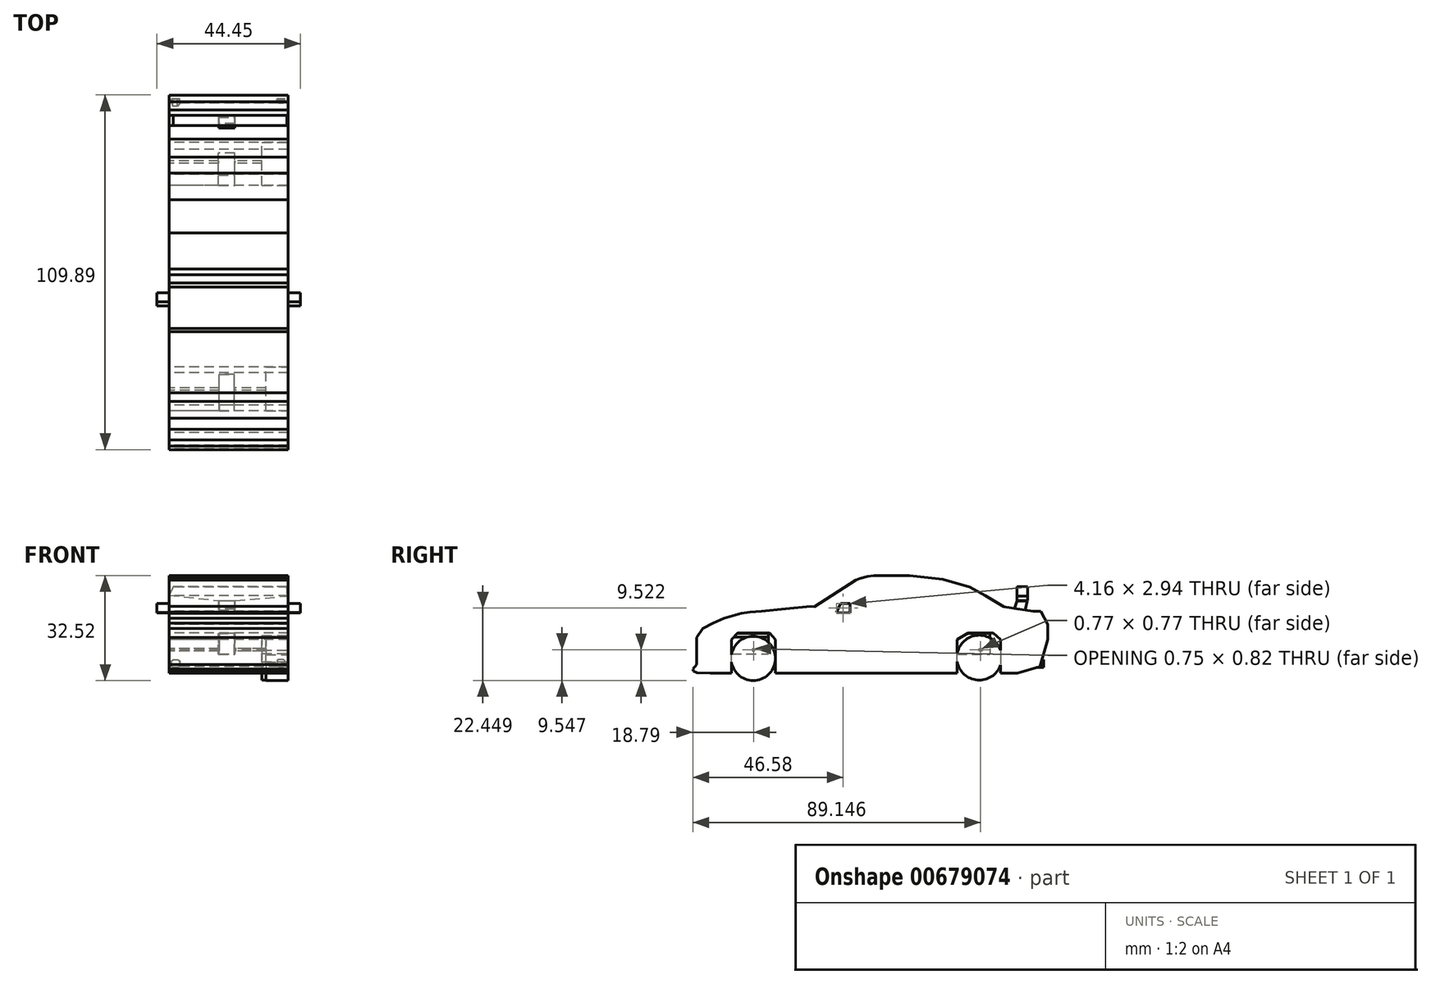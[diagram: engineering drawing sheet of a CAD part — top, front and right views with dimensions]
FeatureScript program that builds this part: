
annotation { "Feature Type Name" : "Feature", "Feature Type Description" : "" }
export const myFeature = defineFeature(function(context is Context, id is Id, definition is map)
    precondition{}
    {
        {
            var Q0;
            Q0=qCreatedBy(makeId("Right.planeOp"),FACE);
            var sketch = newSketch(context, id + "F0", { "sketchPlane" : qUnion([Q0])});
            skLineSegment(sketch, "E0", {"start": v(53.3, 2.94) * mm, "end": v(60.21, 4.98) * mm});
            skLineSegment(sketch, "E1", {"start": v(60.21, 4.98) * mm, "end": v(62.65, 13.3) * mm});
            skLineSegment(sketch, "E2", {"start": v(58.05, 22.1) * mm, "end": v(52.83, 22.89) * mm});
            skLineSegment(sketch, "E3", {"start": v(43.36, 26.9) * mm, "end": v(38.48, 29.55) * mm});
            skLineSegment(sketch, "E4", {"start": v(38.48, 29.55) * mm, "end": v(30.16, 31.98) * mm});
            skLineSegment(sketch, "E5", {"start": v(30.16, 31.98) * mm, "end": v(19.87, 33.17) * mm});
            skLineSegment(sketch, "E6", {"start": v(19.87, 33.17) * mm, "end": v(8.77, 33.17) * mm});
            skLineSegment(sketch, "E7", {"start": v(8.77, 33.17) * mm, "end": v(6.96, 32.93) * mm});
            skLineSegment(sketch, "E8", {"start": v(6.96, 32.93) * mm, "end": v(4.48, 32.32) * mm});
            skLineSegment(sketch, "E9", {"start": v(4.48, 32.32) * mm, "end": v(3.18, 31.74) * mm});
            skLineSegment(sketch, "E10", {"start": v(-26.9, 22.15) * mm, "end": v(-32.22, 21.43) * mm});
            skLineSegment(sketch, "E11", {"start": v(-32.22, 21.43) * mm, "end": v(-37.52, 19.89) * mm});
            skLineSegment(sketch, "E12", {"start": v(-39.67, 2.94) * mm, "end": v(-41.9, 2.94) * mm});
            skLineSegment(sketch, "E13", {"start": v(58.05, 22.1) * mm, "end": v(58.25, 23.46) * mm});
            skLineSegment(sketch, "E14", {"start": v(58.25, 23.46) * mm, "end": v(53.04, 24.24) * mm});
            skLineSegment(sketch, "E15", {"start": v(53.04, 24.24) * mm, "end": v(52.83, 22.89) * mm});
            skPoint(sketch, "E16.endSnap0", {"position": v(40.92, 28.23) * mm});
            skPoint(sketch, "E17.start.orphan", {"position": v(61.15, 28.23) * mm});
            skLineSegment(sketch, "E18", {"start": v(-31.65, 2.94) * mm, "end": v(-31.65, 2.94) * mm});
            skLineSegment(sketch, "E19", {"start": v(-39.67, 2.94) * mm, "end": v(-35.23, 2.94) * mm});
            skLineSegment(sketch, "E20", {"start": v(-35.23, 2.94) * mm, "end": v(-35.23, 13.3) * mm});
            skLineSegment(sketch, "E21", {"start": v(-35.23, 13.3) * mm, "end": v(-33.4, 15.33) * mm});
            skLineSegment(sketch, "E22", {"start": v(-33.4, 15.33) * mm, "end": v(-23.45, 15.33) * mm});
            skLineSegment(sketch, "E23", {"start": v(-23.45, 15.33) * mm, "end": v(-21.63, 13.3) * mm});
            skLineSegment(sketch, "E24", {"start": v(-21.63, 13.3) * mm, "end": v(-21.63, 2.94) * mm});
            skLineSegment(sketch, "E25", {"start": v(-21.63, 2.94) * mm, "end": v(34.62, 2.94) * mm});
            skLineSegment(sketch, "E26", {"start": v(34.62, 2.94) * mm, "end": v(34.62, 13.3) * mm});
            skLineSegment(sketch, "E27", {"start": v(34.62, 13.3) * mm, "end": v(38.08, 15.33) * mm});
            skLineSegment(sketch, "E28", {"start": v(38.08, 15.33) * mm, "end": v(45.8, 15.33) * mm});
            skLineSegment(sketch, "E29", {"start": v(45.8, 15.33) * mm, "end": v(48.03, 13.3) * mm});
            skLineSegment(sketch, "E30", {"start": v(48.03, 13.3) * mm, "end": v(48.03, 2.94) * mm});
            skLineSegment(sketch, "E31", {"start": v(48.03, 2.94) * mm, "end": v(53.3, 2.94) * mm});
            skLineSegment(sketch, "E32", {"start": v(62.65, 13.3) * mm, "end": v(62.65, 18.08) * mm});
            skLineSegment(sketch, "E33", {"start": v(62.65, 18.08) * mm, "end": v(60.52, 22.13) * mm});
            skLineSegment(sketch, "E34", {"start": v(60.52, 22.13) * mm, "end": v(58.05, 22.1) * mm});
            skPoint(sketch, "E35.orphan", {"position": v(49.04, 23.45) * mm});
            skLineSegment(sketch, "E36", {"start": v(43.36, 26.9) * mm, "end": v(49.04, 23.45) * mm});
            skLineSegment(sketch, "E37", {"start": v(52.83, 22.89) * mm, "end": v(49.04, 23.45) * mm});
            skPoint(sketch, "E38.start.orphan", {"position": v(-41.9, 13.3) * mm});
            skLineSegment(sketch, "E39", {"start": v(-37.52, 19.89) * mm, "end": v(-40.96, 18.37) * mm});
            skLineSegment(sketch, "E40", {"start": v(-40.96, 18.37) * mm, "end": v(-44.18, 16.7) * mm});
            skLineSegment(sketch, "E41", {"start": v(-44.18, 16.7) * mm, "end": v(-46.1, 14) * mm});
            skLineSegment(sketch, "E42", {"start": v(-46.1, 14) * mm, "end": v(-46.1, 7.62) * mm});
            skLineSegment(sketch, "E43", {"start": v(-46.1, 7.62) * mm, "end": v(-46.1, 5.6) * mm});
            skLineSegment(sketch, "E44", {"start": v(-46.1, 5.6) * mm, "end": v(-47.24, 4.24) * mm});
            skLineSegment(sketch, "E45", {"start": v(-47.24, 4.24) * mm, "end": v(-47.06, 3.62) * mm});
            skLineSegment(sketch, "E46", {"start": v(-47.06, 3.62) * mm, "end": v(-45.9, 3.1) * mm});
            skLineSegment(sketch, "E47", {"start": v(-45.9, 3.1) * mm, "end": v(-41.9, 2.94) * mm});
            skPoint(sketch, "E48.end.orphan", {"position": v(-8.55, 23.45) * mm});
            skLineSegment(sketch, "E49", {"start": v(-29.56, 21.79) * mm, "end": v(-25.96, 22.15) * mm});
            skLineSegment(sketch, "E50", {"start": v(-25.96, 22.15) * mm, "end": v(-18.53, 22.9) * mm});
            skLineSegment(sketch, "E51", {"start": v(-18.53, 22.9) * mm, "end": v(-10.75, 23.63) * mm});
            skLineSegment(sketch, "E52", {"start": v(-10.75, 23.63) * mm, "end": v(-9.64, 23.45) * mm});
            skLineSegment(sketch, "E53", {"start": v(-9.64, 23.45) * mm, "end": v(3.18, 31.74) * mm});
            skSolve(sketch);
        }
        {
            var Q0;
            Q0=makeQuery(id+"F0.imprint","IMPRINT",FACE,{"disambiguationData":[TD([[makeQuery(id+"F0.imprint","IMPRINT",EDGE,{"derivedFrom":sQuery(id+"F0.wireOp",EDGE,"E0")}),1.0]])]});
            extrude(context, id + "F1", {"entities" : qUnion([Q0]), "depth" : 36.83 * mm, "offsetDistance" : 25.4 * mm});
        }
        {
            var Q0;
            Q0=qCreatedBy(makeId("Front.planeOp"),FACE);
            cPlane(context, id + "F2", {"entities" : qUnion([Q0]), "cplaneType" : CPlaneType.OFFSET, "offset" : 56.4 * mm, "oppositeDirection" : true, "width" : 152.4 * mm, "height" : 152.4 * mm});
        }
        {
            var Q0;
            Q0=qCreatedBy(id+"F2.planeOp",FACE);
            var sketch = newSketch(context, id + "F3", { "sketchPlane" : qUnion([Q0])});
            skLineSegment(sketch, "E54", {"start": v(20.45, 25.35) * mm, "end": v(36.66, 26.84) * mm});
            skLineSegment(sketch, "E55", {"start": v(36.66, 26.84) * mm, "end": v(36.4, 29.7) * mm});
            skLineSegment(sketch, "E56", {"start": v(36.4, 29.7) * mm, "end": v(1.22, 29.7) * mm});
            skLineSegment(sketch, "E57", {"start": v(1.22, 29.7) * mm, "end": v(0, 27.1) * mm});
            skLineSegment(sketch, "E58", {"start": v(0, 27.1) * mm, "end": v(15.49, 25.34) * mm});
            skLineSegment(sketch, "E59", {"start": v(15.49, 25.34) * mm, "end": v(20.45, 25.35) * mm});
            skSolve(sketch);
        }
        {
            var Q0;
            Q0=makeQuery(id+"F3.imprint","IMPRINT",FACE,{"disambiguationData":[TD([[makeQuery(id+"F3.imprint","IMPRINT",EDGE,{"derivedFrom":sQuery(id+"F3.wireOp",EDGE,"E54")}),1.0]])]});
            var Q1;
            Q1=makeQuery(id+"F1.opExtrude","SWEPT_FACE",FACE,{"disambiguationData":[OSD([sQuery(id+"F0.wireOp",EDGE,"E3")])]});
            extrude(context, id + "F4", {"entities" : qUnion([Q0, Q1]), "operationType" : NewBodyOperationType.ADD, "depth" : 3.23 * mm, "offsetDistance" : 25.4 * mm});
        }
        {
            var Q0;
            Q0=qCreatedBy(makeId("Right.planeOp"),FACE);
            cPlane(context, id + "F5", {"entities" : qUnion([Q0]), "cplaneType" : CPlaneType.OFFSET, "offset" : 17.78 * mm, "width" : 152.4 * mm, "height" : 152.4 * mm});
        }
        {
            var Q0;
            Q0=qCreatedBy(id+"F5.planeOp",FACE);
            var sketch = newSketch(context, id + "F6", { "sketchPlane" : qUnion([Q0])});
            skLineSegment(sketch, "E60", {"start": v(52.4, 23) * mm, "end": v(53.2, 25.33) * mm});
            skLineSegment(sketch, "E61", {"start": v(53.2, 25.33) * mm, "end": v(56.35, 25.33) * mm});
            skLineSegment(sketch, "E62", {"start": v(56.35, 25.33) * mm, "end": v(55.74, 22.39) * mm});
            skLineSegment(sketch, "E63", {"start": v(55.74, 22.39) * mm, "end": v(52.4, 23) * mm});
            skSolve(sketch);
        }
        {
            var Q0;
            Q0=makeQuery(id+"F6.imprint","IMPRINT",FACE,{"disambiguationData":[TD([[makeQuery(id+"F6.imprint","IMPRINT",EDGE,{"derivedFrom":sQuery(id+"F6.wireOp",EDGE,"E60")}),-1.0]])]});
            var Q1;
            Q1 = qSketchRegion(id + "F6", true);
            extrude(context, id + "F7", {"entities" : qUnion([Q0, Q1]), "operationType" : NewBodyOperationType.ADD, "depth" : 2.46 * mm, "offsetDistance" : 25.4 * mm, "hasSecondDirection" : true, "secondDirectionOppositeDirection" : true, "secondDirectionDepth" : 2.46 * mm});
        }
        {
            var Q0;
            Q0=qCreatedBy(id+"F5.planeOp",FACE);
            cPlane(context, id + "F8", {"entities" : qUnion([Q0]), "cplaneType" : CPlaneType.OFFSET, "offset" : 19.05 * mm, "width" : 152.4 * mm, "height" : 152.4 * mm});
        }
        {
            var Q0;
            Q0=qCreatedBy(id+"F8.planeOp",FACE);
            var sketch = newSketch(context, id + "F9", { "sketchPlane" : qUnion([Q0])});
            skLineSegment(sketch, "E64", {"start": v(-2.74, 21.73) * mm, "end": v(-1.42, 24.57) * mm});
            skLineSegment(sketch, "E65", {"start": v(-1.42, 24.57) * mm, "end": v(1.42, 24.57) * mm});
            skLineSegment(sketch, "E66", {"start": v(1.42, 24.57) * mm, "end": v(1.42, 21.63) * mm});
            skLineSegment(sketch, "E67", {"start": v(1.42, 21.63) * mm, "end": v(-2.74, 21.73) * mm});
            skSolve(sketch);
        }
        {
            var Q0;
            Q0 = qSketchRegion(id + "F9", true);
            extrude(context, id + "F10", {"entities" : qUnion([Q0]), "operationType" : NewBodyOperationType.ADD, "depth" : 3.8 * mm, "offsetDistance" : 25.4 * mm, "hasSecondDirection" : true, "secondDirectionOppositeDirection" : true, "secondDirectionDepth" : 40.64 * mm});
        }
        {
            var Q0;
            Q0=qCreatedBy(id+"F2.planeOp",FACE);
            cPlane(context, id + "F11", {"entities" : qUnion([Q0]), "cplaneType" : CPlaneType.OFFSET, "offset" : 14.48 * mm, "width" : 152.4 * mm, "height" : 152.4 * mm});
        }
        {
            var Q0;
            Q0=qCreatedBy(id+"F11.planeOp",FACE);
            var sketch = newSketch(context, id + "F12", { "sketchPlane" : qUnion([Q0])});
            skLineSegment(sketch, "E68", {"start": v(20.26, 9.91) * mm, "end": v(20.26, 15.2) * mm});
            skLineSegment(sketch, "E69", {"start": v(20.26, 15.2) * mm, "end": v(15.23, 15.2) * mm});
            skLineSegment(sketch, "E70", {"start": v(15.23, 15.2) * mm, "end": v(15.23, 9.91) * mm});
            skLineSegment(sketch, "E71", {"start": v(20.26, 9.91) * mm, "end": v(20.26, 8.77) * mm});
            skLineSegment(sketch, "E72", {"start": v(20.26, 8.77) * mm, "end": v(15.23, 8.77) * mm});
            skLineSegment(sketch, "E73", {"start": v(15.23, 8.77) * mm, "end": v(15.23, 9.91) * mm});
            skSolve(sketch);
        }
        {
            var Q0;
            Q0 = qSketchRegion(id + "F12", true);
            extrude(context, id + "F13", {"entities" : qUnion([Q0]), "operationType" : NewBodyOperationType.ADD, "depth" : 7.37 * mm, "offsetDistance" : 25.4 * mm, "hasSecondDirection" : true, "secondDirectionOppositeDirection" : true, "secondDirectionDepth" : 2.8 * mm});
        }
        {
            var Q0;
            Q0=qCreatedBy(makeId("Front.planeOp"),FACE);
            cPlane(context, id + "F14", {"entities" : qUnion([Q0]), "cplaneType" : CPlaneType.OFFSET, "offset" : 28.45 * mm, "width" : 152.4 * mm, "height" : 152.4 * mm});
        }
        {
            var Q0;
            Q0=qCreatedBy(id+"F14.planeOp",FACE);
            var sketch = newSketch(context, id + "F15", { "sketchPlane" : qUnion([Q0])});
            skLineSegment(sketch, "E74", {"start": v(20.18, 14.1) * mm, "end": v(20.18, 8.89) * mm});
            skLineSegment(sketch, "E75", {"start": v(20.18, 8.89) * mm, "end": v(15.49, 8.89) * mm});
            skLineSegment(sketch, "E76", {"start": v(15.49, 8.89) * mm, "end": v(15.49, 14.1) * mm});
            skLineSegment(sketch, "E77", {"start": v(15.49, 14.1) * mm, "end": v(15.49, 15.27) * mm});
            skLineSegment(sketch, "E78", {"start": v(15.49, 15.27) * mm, "end": v(20.17, 15.27) * mm});
            skLineSegment(sketch, "E79", {"start": v(20.17, 15.27) * mm, "end": v(20.18, 14.1) * mm});
            skSolve(sketch);
        }
        {
            var Q0;
            Q0 = qSketchRegion(id + "F15", true);
            extrude(context, id + "F16", {"entities" : qUnion([Q0]), "operationType" : NewBodyOperationType.ADD, "depth" : 7.37 * mm, "offsetDistance" : 25.4 * mm, "hasSecondDirection" : true, "secondDirectionOppositeDirection" : true, "secondDirectionDepth" : 4.57 * mm});
        }
        {
            var Q0;
            Q0=qCreatedBy(id+"F5.planeOp",FACE);
            var sketch = newSketch(context, id + "F17", { "sketchPlane" : qUnion([Q0])});
            skLineSegment(sketch, "E80", {"start": v(-28.44, 10.6) * mm, "end": v(-28.82, 10.6) * mm});
            skLineSegment(sketch, "E81", {"start": v(-28.82, 10.6) * mm, "end": v(-28.82, 10.17) * mm});
            skLineSegment(sketch, "E82", {"start": v(-28.82, 10.17) * mm, "end": v(-28.82, 9.79) * mm});
            skLineSegment(sketch, "E83", {"start": v(-28.82, 9.79) * mm, "end": v(-28.45, 9.79) * mm});
            skLineSegment(sketch, "E84", {"start": v(-28.45, 9.79) * mm, "end": v(-28.08, 9.79) * mm});
            skLineSegment(sketch, "E85", {"start": v(-28.08, 9.79) * mm, "end": v(-28.08, 10.17) * mm});
            skLineSegment(sketch, "E86", {"start": v(-28.44, 10.6) * mm, "end": v(-28.09, 10.6) * mm});
            skLineSegment(sketch, "E87", {"start": v(-28.09, 10.6) * mm, "end": v(-28.08, 10.17) * mm});
            skSolve(sketch);
        }
        {
            var Q0;
            Q0 = qSketchRegion(id + "F17", true);
            extrude(context, id + "F18", {"entities" : qUnion([Q0]), "operationType" : NewBodyOperationType.ADD, "depth" : 19.05 * mm, "offsetDistance" : 25.4 * mm, "hasSecondDirection" : true, "secondDirectionOppositeDirection" : true, "secondDirectionDepth" : 17.78 * mm});
        }
        {
            var Q0;
            Q0=qCreatedBy(id+"F5.planeOp",FACE);
            var sketch = newSketch(context, id + "F19", { "sketchPlane" : qUnion([Q0])});
            skLineSegment(sketch, "E88", {"start": v(41.9, 10.56) * mm, "end": v(42.3, 10.56) * mm});
            skLineSegment(sketch, "E89", {"start": v(42.3, 10.56) * mm, "end": v(42.3, 10.18) * mm});
            skLineSegment(sketch, "E90", {"start": v(42.3, 10.18) * mm, "end": v(42.3, 9.78) * mm});
            skLineSegment(sketch, "E91", {"start": v(42.3, 9.78) * mm, "end": v(41.9, 9.78) * mm});
            skLineSegment(sketch, "E92", {"start": v(41.9, 9.78) * mm, "end": v(41.52, 9.78) * mm});
            skLineSegment(sketch, "E93", {"start": v(41.52, 9.78) * mm, "end": v(41.52, 10.56) * mm});
            skLineSegment(sketch, "E94", {"start": v(41.52, 10.56) * mm, "end": v(41.9, 10.56) * mm});
            skSolve(sketch);
        }
        {
            var Q0;
            Q0 = qSketchRegion(id + "F19", true);
            extrude(context, id + "F20", {"entities" : qUnion([Q0]), "operationType" : NewBodyOperationType.ADD, "depth" : 19.05 * mm, "offsetDistance" : 25.4 * mm, "hasSecondDirection" : true, "secondDirectionOppositeDirection" : true, "secondDirectionDepth" : 17.78 * mm});
        }
        {
            var Q0;
            Q0=qCreatedBy(id+"F2.planeOp",FACE);
            cPlane(context, id + "F21", {"entities" : qUnion([Q0]), "cplaneType" : CPlaneType.OFFSET, "offset" : 5.08 * mm, "oppositeDirection" : true, "width" : 152.4 * mm, "height" : 152.4 * mm});
        }
        {
            var Q0;
            Q0=qCreatedBy(id+"F21.planeOp",FACE);
            var sketch = newSketch(context, id + "F22", { "sketchPlane" : qUnion([Q0])});
            skLineSegment(sketch, "E95", {"start": v(35.75, 6.7) * mm, "end": v(35.75, 5.26) * mm});
            skLineSegment(sketch, "E96", {"start": v(35.75, 5.26) * mm, "end": v(35.28, 4.97) * mm});
            skLineSegment(sketch, "E97", {"start": v(35.28, 4.97) * mm, "end": v(33.86, 4.97) * mm});
            skLineSegment(sketch, "E98", {"start": v(33.86, 4.97) * mm, "end": v(33.33, 5.26) * mm});
            skLineSegment(sketch, "E99", {"start": v(33.33, 5.26) * mm, "end": v(33.33, 6.73) * mm});
            skLineSegment(sketch, "E100", {"start": v(33.33, 6.73) * mm, "end": v(33.66, 7.08) * mm});
            skLineSegment(sketch, "E101", {"start": v(33.66, 7.08) * mm, "end": v(35.33, 7.08) * mm});
            skLineSegment(sketch, "E102", {"start": v(35.33, 7.08) * mm, "end": v(35.75, 6.7) * mm});
            skLineSegment(sketch, "E103", {"start": v(3.24, 6.77) * mm, "end": v(2.58, 7.08) * mm});
            skLineSegment(sketch, "E104", {"start": v(2.58, 7.08) * mm, "end": v(1.28, 7.08) * mm});
            skLineSegment(sketch, "E105", {"start": v(1.28, 7.08) * mm, "end": v(0.73, 6.68) * mm});
            skLineSegment(sketch, "E106", {"start": v(0.73, 6.68) * mm, "end": v(0.73, 5.14) * mm});
            skLineSegment(sketch, "E107", {"start": v(0.73, 5.14) * mm, "end": v(1.16, 4.65) * mm});
            skLineSegment(sketch, "E108", {"start": v(1.16, 4.65) * mm, "end": v(2.45, 4.65) * mm});
            skLineSegment(sketch, "E109", {"start": v(2.45, 4.65) * mm, "end": v(3.24, 4.94) * mm});
            skLineSegment(sketch, "E110", {"start": v(3.24, 4.94) * mm, "end": v(3.24, 6.77) * mm});
            skPoint(sketch, "E111.orphan", {"position": v(3.37, 6.7) * mm});
            skSolve(sketch);
        }
        {
            var Q0;
            Q0 = qSketchRegion(id + "F22", true);
            extrude(context, id + "F23", {"entities" : qUnion([Q0]), "operationType" : NewBodyOperationType.ADD, "depth" : 3.2 * mm, "offsetDistance" : 25.4 * mm});
        }
        {
            var Q0;
            Q0=qCreatedBy(id+"F8.planeOp",FACE);
            var sketch = newSketch(context, id + "F24", { "sketchPlane" : qUnion([Q0])});
            skCircle(sketch, "E112", {"center": v(-28.5, 7.5) * mm, "radius": 6.85 * mm});
            skSolve(sketch);
        }
        {
            var Q0;
            Q0 = qSketchRegion(id + "F24", true);
            extrude(context, id + "F25", {"entities" : qUnion([Q0]), "operationType" : NewBodyOperationType.ADD, "oppositeDirection" : true, "depth" : 6.86 * mm, "offsetDistance" : 25.4 * mm});
        }
        {
            var Q0;
            Q0=qCreatedBy(id+"F8.planeOp",FACE);
            var sketch = newSketch(context, id + "F26", { "sketchPlane" : qUnion([Q0])});
            skCircle(sketch, "E113", {"center": v(41.46, 7.72) * mm, "radius": 6.95 * mm});
            skSolve(sketch);
        }
        {
            var Q0;
            Q0=makeQuery(id+"F26.imprint","IMPRINT",FACE,{"disambiguationData":[TD([[makeQuery(id+"F26.imprint","IMPRINT",EDGE,{"derivedFrom":sQuery(id+"F26.wireOp",EDGE,"E113")}),1.0]])]});
            extrude(context, id + "F27", {"entities" : qUnion([Q0]), "operationType" : NewBodyOperationType.ADD, "oppositeDirection" : true, "depth" : 8.13 * mm, "offsetDistance" : 25.4 * mm});
        }
    });
